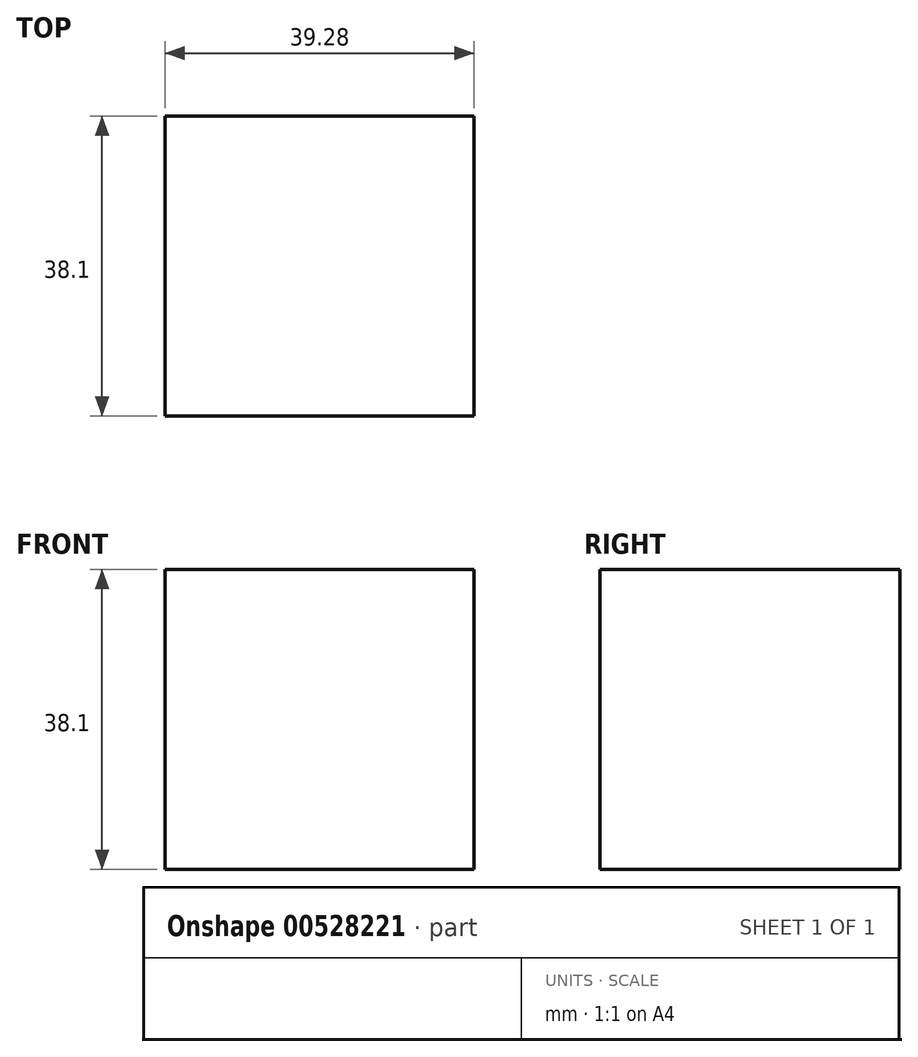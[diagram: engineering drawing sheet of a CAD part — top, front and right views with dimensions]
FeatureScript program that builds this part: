
annotation { "Feature Type Name" : "Feature", "Feature Type Description" : "" }
export const myFeature = defineFeature(function(context is Context, id is Id, definition is map)
    precondition{}
    {
        {
            var Q0;
            Q0=qCreatedBy(makeId("Top.planeOp"),FACE);
            var sketch = newSketch(context, id + "F0", { "sketchPlane" : qUnion([Q0])});
            skLineSegment(sketch, "E0", {"start": v(-81.2, 38.1) * mm, "end": v(-81.2, 0) * mm});
            skLineSegment(sketch, "E1", {"start": v(-81.2, 38.1) * mm, "end": v(-41.66, 38.1) * mm});
            skLineSegment(sketch, "E2.bottom", {"start": v(-81.2, 38.1) * mm, "end": v(-41.9, 38.1) * mm});
            skLineSegment(sketch, "E2.top", {"start": v(-81.2, 0) * mm, "end": v(-41.9, 0) * mm});
            skLineSegment(sketch, "E2.right", {"start": v(-41.9, 38.1) * mm, "end": v(-41.9, 0) * mm});
            skSolve(sketch);
        }
        {
            var Q0;
            Q0 = qSketchRegion(id + "F0", true);
            extrude(context, id + "F1", {"entities" : qUnion([Q0]), "depth" : 38.1 * mm, "offsetDistance" : 25.4 * mm});
        }
    });
